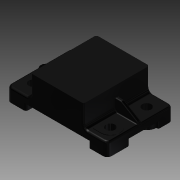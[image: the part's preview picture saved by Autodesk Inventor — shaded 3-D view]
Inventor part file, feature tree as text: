
AUTODESK INVENTOR PART (.ipt)
format: ipt  version: 2013 (Build 170138000, 138)  size: 527,360 bytes
history: native  units: mm (DEFAULTED — no unit token found)
features: sketch x12, extrude x11, fillet x5, plane x4, mirror x3, rib x1
ambient origin geometry x8: Origin, YZ Plane, XZ Plane, XY Plane, X Axis, Y Axis, Z Axis, Center Point
bodies: Solid1 (feature_tree)
feature tree (36):
  extrude  "Extrusion1"  Depth=5.08mm
  fillet  "Fillet19"  Radius=73.66mm
  plane  "Work Plane6"
  plane  "Work Plane7"
  extrude  "Extrusion4"  Depth=48.26mm TaperAngle=0.0deg
  fillet  "Fillet20"  Radius=3.048mm
  extrude  "Extrusion10"  Depth=1.524mm
  extrude  "Extrusion12"  Depth=8.89mm TaperAngle=0.0deg
  fillet  "Fillet21"  Radius=0.381mm
  plane  "Work Plane3"
  plane  "Work Plane4"
  mirror  "Mirror4"
  mirror  "Mirror5"
  extrude  "Extrusion11"  Depth=3.302mm
  extrude  "Extrusion13"  Depth=8.636mm
  extrude  "Extrusion14"  Depth=2.54mm
  extrude  "Extrusion15"  Depth=0.762mm
  extrude  "Extrusion16"  Depth=3.048mm
  extrude  "Extrusion5"  Depth=13.97mm
  extrude  "Extrusion6"  Depth=4.826mm TaperAngle=0.0deg
  rib  "Rib2"
  fillet  "Fillet22"  Radius=1.27mm
  fillet  "Fillet23"  Radius=4.826mm
  mirror  "Mirror6"
  sketch  "Sketch1"  dims[d1=21.336mm d2=5.08mm d3=73.66mm]
  sketch  "Sketch5"  dims[d4=38.862mm d5=48.26mm d6=0.0mm d40=3.048mm]
  sketch  "Sketch6"  dims[d41=3.048mm d42=1.524mm]
  sketch  "Sketch7"  dims[d43=6.604mm d46=8.89mm d47=0.0mm d48=0.381mm d49=0.0mm]
  sketch  "Sketch8"  dims[d50=0.381mm d51=0.0mm d52=3.302mm]
  sketch  "Sketch14"  dims[d53=3.302mm d54=8.636mm]
  sketch  "Sketch15"  dims[d55=3.302mm d56=2.54mm]
  sketch  "Sketch16"  dims[d57=2.54mm d58=0.762mm]
  sketch  "Sketch17"  dims[d59=0.762mm d83=3.048mm]
  sketch  "Sketch18"  dims[d84=1.524mm d85=13.97mm]
  sketch  "Sketch19"  dims[d86=16.51mm d87=4.826mm d88=0.0mm d89=1.27mm d90=4.826mm d91=0.0mm]
  sketch  "Sketch20"  dims[d92=3.048mm d93=1.524mm d94=16.51mm d95=13.97mm d96=4.826mm d97=0.0mm d98=1.27mm d99=4.826mm d100=0.0mm d101=13.97mm d102=13.97mm d103=3.048mm d104=1.524mm d105=1.016mm d106=3.048mm d107=1.524mm d108=1.016mm d109=13.97mm d110=4.826mm d111=0.0mm d112=1.27mm d113=1.27mm d114=0.381mm d116=0.381mm d117=13.97mm d118=4.826mm d119=0.0mm d120=1.27mm d121=0.381mm d122=0.381mm d124=13.97mm d125=4.826mm d126=0.0mm d127=13.335mm d128=28.321mm]
